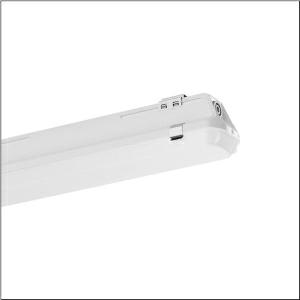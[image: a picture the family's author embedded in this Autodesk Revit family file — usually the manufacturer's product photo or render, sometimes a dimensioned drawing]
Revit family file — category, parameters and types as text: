
# Revit family: monsun_r__11_51fp20mp480h_c015
name_source: partatom
category: Lighting Fixtures
units: mm (PartAtom-declared; Revit-internal decimal feet)

## family parameters
Cut with Voids When Loaded = No
Host = Face
Light Source = No
Part Type = Normal
Room Calculation Point = No
Round Connector Dimension = Use Diameter
Shared = No

## types (1)
- --- (1 x LED, 8220 lm, 52.3 W, 4000K)
    Apparent Load = 52 VA
    CIE Flux Codes = 45 75 93 94 100
    Color Rendering = 80
    Color Temperature = 4000K
    Default Elevation = 1800 mm
    Description = Monsun® 11, damp-proof luminaire, chain hanger, primary optical cover: enclosure, of PC, light emission: direct distribution, primary light characteristic: symmetric, installation type: suspended mounting, surface-mounted, horizontal mounting, vertical mounting, LED, rated luminous flux: 8.220lm, luminous efficacy: 157lm/W, light colour: 840, colour temperature: 4000K, control gear: ECG, with terminal, 3-pole, max. 2.5mm², mains connection: 220..240V, AC, 50/60Hz, rated input power: 52W, luminaire housing, of glass-fibre reinforced polyester, uncoated, bright grey, incl. chain hanger, length: 1.590mm, width: 90mm, height: 88mm, clip for enclosure, of stainless steel (V2A), ceiling mounting element, of stainless steel (V2A), chain hanger, of stainless steel (V2A), protection rating (complete): IP66, insulation class (complete): insulation class I (protective earthing), certification: CE, ENEC, VDE, UKCA, protection symbol: D, impact resistance: IK08, permissible operating ambient temperature: -35..+40°C, standard: EN 50419, EN 60598-2-1, no direct snow, no direct sun, no direct rain, for indoor or canopied outdoor use, corresponds to IFS (International Featured Standards) requirements for safety and quality in the food industry, contact your sales advisor before using the luminaires in applications with unclear chemical exposure, large temperature fluctuations or condensation-forming humidity, LABS conformity tested according to VDMA 24364:2018-05, packaging unit: 1 piece
    Height = 89 mm
    Lamp = 1 x LED
    Lamp Light Flux = 8220 lm
    Lamp Power = 52.3 W
    Lamp count = 1
    Length = 1590 mm
    Luminous efficacy = 157 lm/W
    Manufacturer = Siteco
    ModVariant = No
    Model = 51FP20MP480H
    Mounting Place = Ceiling
    Mounting Type = Surface mounted
    Number of Poles = 1
    OnlyDefault = Yes
    Power Factor = 1
    Product Name = Monsun® 11
    Product group = damp-proof luminaire
    ProductGroupID = 300
    Protection Class = Protection class I
    Protection Degree = IP 66
    RLX_Detail_Level = 1
    RLX_Emergency_Light_Flux = 0 lm
    RLX_Emergency_Type = 0
    RLX_Emergency_Type_DB = No
    RlxData = <blob elided: 90001 chars, md5=eeaf8be8>
    Socket = socket
    Standby Power = 0 W
    System Light Flux = 8220 lm
    System Power = 52 W
    Type Comments = factory setting: luminous flux: 100 % | (A | C | E) | 120 mA
    Type Image = l_1319650.jpg
    URL = http://relux.com
    VarID = @adj_174187
    Voltage = 0 V
    Weight = 0.00 kg
    Width = 90 mm

## geometry (parser evidence)
native form markers: Blend x4, Sweep x14
no freeform markers — native parametric forms only
